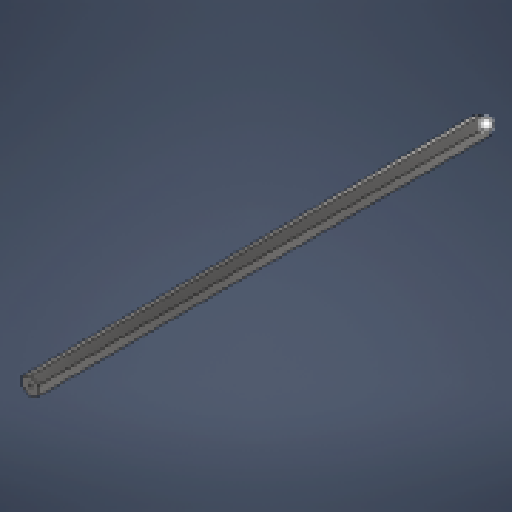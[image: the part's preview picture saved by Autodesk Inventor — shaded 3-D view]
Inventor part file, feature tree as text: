
AUTODESK INVENTOR PART (.ipt)
format: ipt  version: 2024.3 (Build 283343000, 343)  size: 167,424 bytes
history: native  units: in
note: dims shown in document units (in); Inventor stores cm internally (conversion verified against a paired STEP export)
features: extrude x1, sketch x1
ambient origin geometry x8: Origin, YZ Plane, XZ Plane, XY Plane, X Axis, Y Axis, Z Axis, Center Point
bodies: Body1 (feature_tree)
feature tree (2):
  extrude  "Extrusion1"  Depth=14.0in TaperAngle=0.0deg
  sketch  "Sketch1"  dims[d0=0.5in d1=14.0in d2=0.0in d3=0.112in d4=0.0in]
